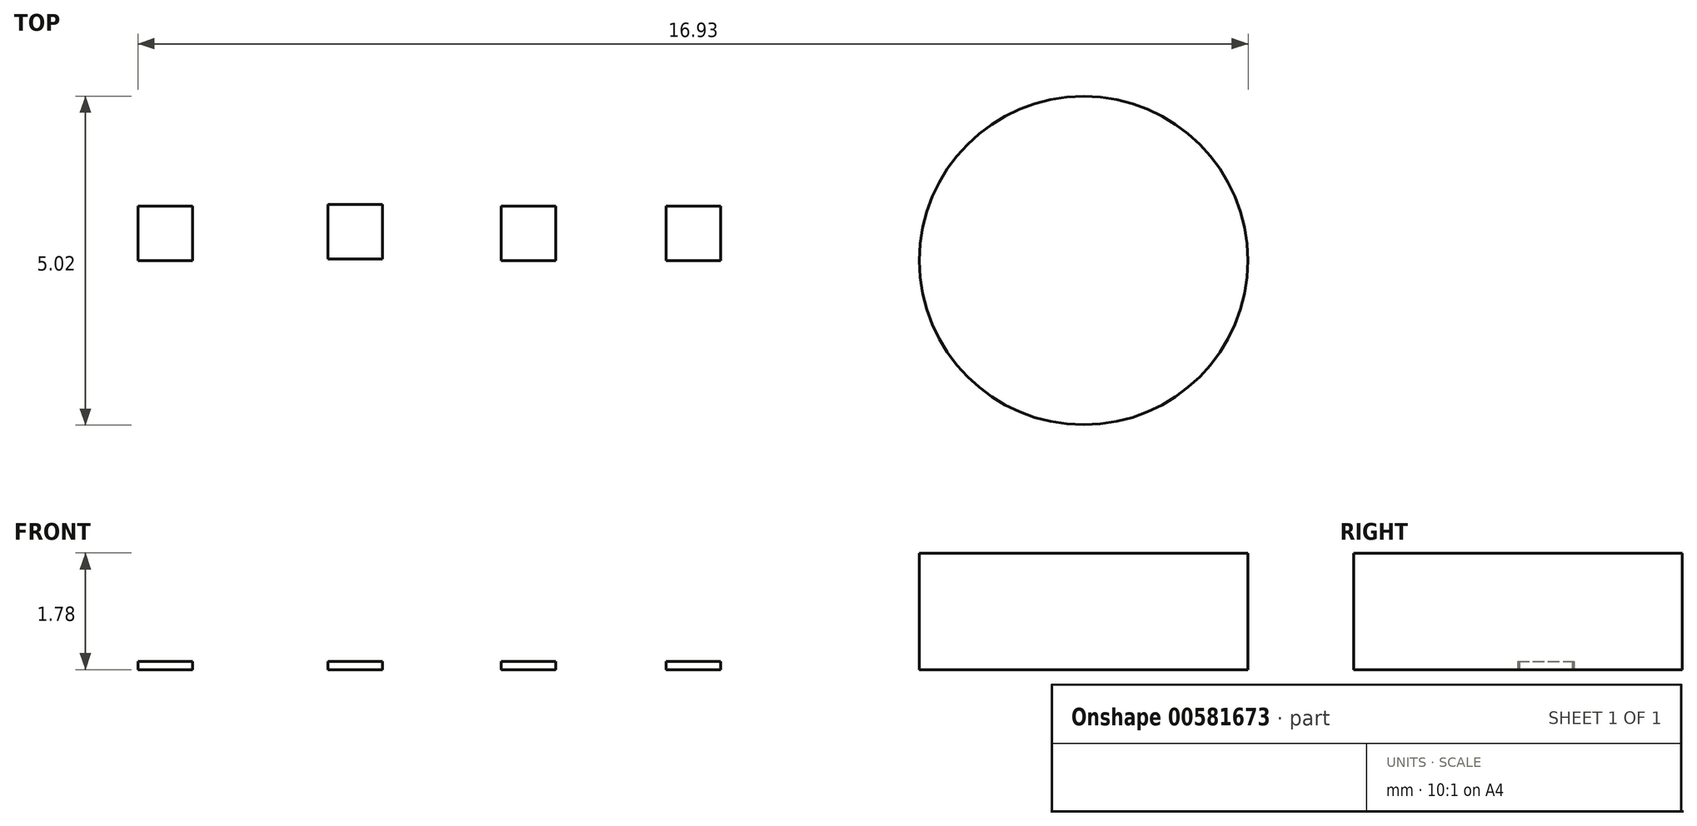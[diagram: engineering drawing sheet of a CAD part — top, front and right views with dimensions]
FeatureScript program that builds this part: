
annotation { "Feature Type Name" : "Feature", "Feature Type Description" : "" }
export const myFeature = defineFeature(function(context is Context, id is Id, definition is map)
    precondition{}
    {
        {
            var Q0;
            Q0=qCreatedBy(makeId("Top.planeOp"),FACE);
            var sketch = newSketch(context, id + "F0", { "sketchPlane" : qUnion([Q0])});
            skCircle(sketch, "E0", {"center": v(0, 0) * mm, "radius": 2.5 * mm});
            skSolve(sketch);
        }
        {
            var Q0;
            Q0 = qSketchRegion(id + "F0", true);
            extrude(context, id + "F1", {"entities" : qUnion([Q0]), "depth" : 1.78 * mm, "offsetDistance" : 25.4 * mm});
        }
        {
            var Q0;
            Q0=qCreatedBy(makeId("Top.planeOp"),FACE);
            var sketch = newSketch(context, id + "F2", { "sketchPlane" : qUnion([Q0])});
            skLineSegment(sketch, "E1.bottom", {"start": v(-5.54, 0) * mm, "end": v(-6.37, 0) * mm});
            skLineSegment(sketch, "E1.top", {"start": v(-5.54, 0.83) * mm, "end": v(-6.37, 0.83) * mm});
            skLineSegment(sketch, "E1.left", {"start": v(-5.54, 0) * mm, "end": v(-5.54, 0.83) * mm});
            skLineSegment(sketch, "E1.right", {"start": v(-6.37, 0) * mm, "end": v(-6.37, 0.83) * mm});
            skSolve(sketch);
        }
        {
            var Q0;
            Q0 = qSketchRegion(id + "F2", true);
            extrude(context, id + "F3", {"entities" : qUnion([Q0]), "depth" : 0.13 * mm, "offsetDistance" : 25.4 * mm});
        }
        {
            var Q0;
            Q0=makeQuery(id+"F3.opExtrude","SWEPT_BODY",BODY,{"disambiguationData":[OSD([sQuery(id+"F2.wireOp",EDGE,"E1.bottom"),sQuery(id+"F2.wireOp",EDGE,"E1.top"),sQuery(id+"F2.wireOp",EDGE,"E1.left"),sQuery(id+"F2.wireOp",EDGE,"E1.right")])]});
            transform(context, id + "F4", {"entities" : qUnion([Q0]), "transformType" : TransformType.TRANSLATION_3D, "dx" : -2.5 * mm, "dy" : 0 * mm, "dz" : 0 * mm, "makeCopy" : true});
        }
        {
            var Q0;
            Q0=makeQuery(id+"F3.opExtrude","SWEPT_BODY",BODY,{"disambiguationData":[OSD([sQuery(id+"F2.wireOp",EDGE,"E1.bottom"),sQuery(id+"F2.wireOp",EDGE,"E1.top"),sQuery(id+"F2.wireOp",EDGE,"E1.left"),sQuery(id+"F2.wireOp",EDGE,"E1.right")])]});
            transform(context, id + "F5", {"entities" : qUnion([Q0]), "transformType" : TransformType.TRANSLATION_3D, "dx" : -5.16 * mm, "dy" : 0.03 * mm, "dz" : 0 * mm, "makeCopy" : true});
        }
        {
            var Q0;
            Q0=makeQuery(id+"F3.opExtrude","SWEPT_BODY",BODY,{"disambiguationData":[OSD([sQuery(id+"F2.wireOp",EDGE,"E1.bottom"),sQuery(id+"F2.wireOp",EDGE,"E1.top"),sQuery(id+"F2.wireOp",EDGE,"E1.left"),sQuery(id+"F2.wireOp",EDGE,"E1.right")])]});
            transform(context, id + "F6", {"entities" : qUnion([Q0]), "transformType" : TransformType.TRANSLATION_3D, "dx" : -8.05 * mm, "dy" : 0 * mm, "dz" : 0 * mm, "makeCopy" : true});
        }
    });
